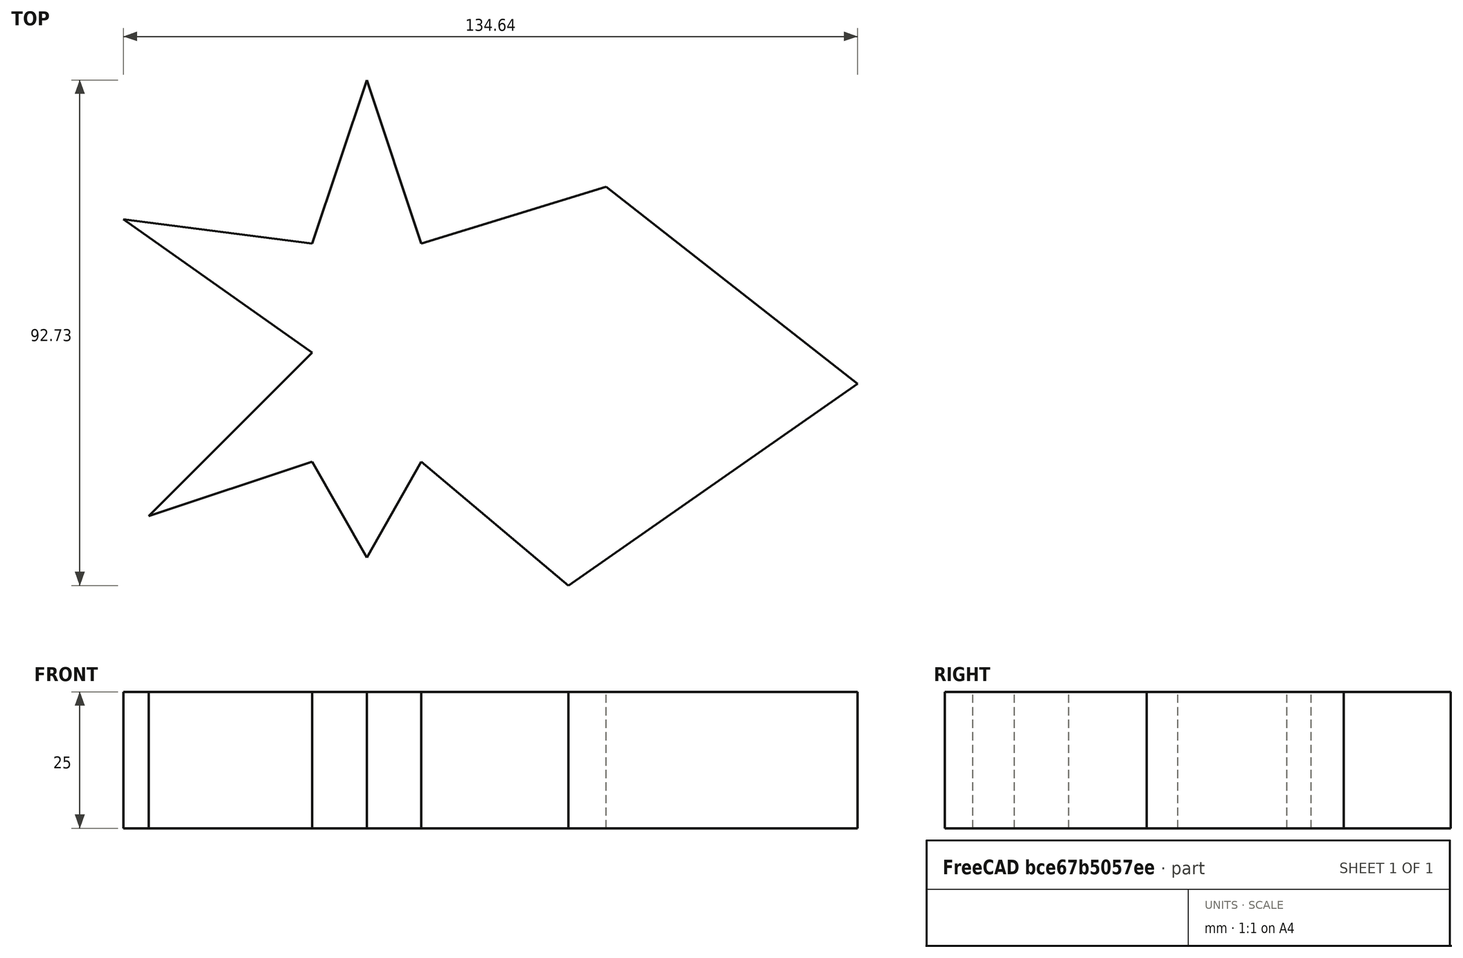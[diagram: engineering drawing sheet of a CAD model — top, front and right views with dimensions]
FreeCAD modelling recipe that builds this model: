
FCSTD DOCUMENT  (FreeCAD 0.18.4R)
Label: tutorial_freecad_ex16_a
License: All rights reserved
LicenseURL: http://en.wikipedia.org/wiki/All_rights_reserved
objects: Sketcher::SketchObject×1, PartDesign::Pad×1, PartDesign::Body×1
note: 4 computed .brp shape members not serialized (recipe doc carries the construction recipe); baked Part::Feature solids carry a one-line shape summary decoded from their .brp

FEATURE [Sketcher::SketchObject] Sketch  label="boceto_estrella"
  MapMode = 5
  Support = -> [XY_Plane]
  sketch-geometry (12):
    g0: LineSegment StartX=0 StartY=50 StartZ=0 EndX=10 EndY=20 EndZ=0
    g1: LineSegment StartX=10 StartY=20 StartZ=0 EndX=43.8533 EndY=30.419 EndZ=0
    g2: LineSegment StartX=43.8533 StartY=30.419 StartZ=0 EndX=90 EndY=-5.74356 EndZ=0
    g3: LineSegment StartX=90 StartY=-5.74356 StartZ=0 EndX=36.976 EndY=-42.7309 EndZ=0
    g4: LineSegment StartX=36.976 StartY=-42.7309 StartZ=0 EndX=10 EndY=-20 EndZ=0
    g5: LineSegment StartX=10 StartY=-20 StartZ=0 EndX=0 EndY=-37.6194 EndZ=0
    g6: LineSegment StartX=0 StartY=-37.6194 StartZ=0 EndX=-10 EndY=-20 EndZ=0
    g7: LineSegment StartX=-10 StartY=-20 StartZ=0 EndX=-40 EndY=-30 EndZ=0
    g8: LineSegment StartX=-40 StartY=-30 StartZ=0 EndX=-10 EndY=0 EndZ=0
    g9: LineSegment StartX=-10 StartY=0 StartZ=0 EndX=-44.6416 EndY=24.4254 EndZ=0
    g10: LineSegment StartX=-44.6416 StartY=24.4254 StartZ=0 EndX=-10 EndY=20 EndZ=0
    g11: LineSegment StartX=-10 StartY=20 StartZ=0 EndX=0 EndY=50 EndZ=0
  constraints (12):
    c: Coincident(g0,g1)
    c: Coincident(g1,g2)
    c: Coincident(g2,g3)
    c: Coincident(g3,g4)
    c: Coincident(g4,g5)
    c: Coincident(g5,g6)
    c: Coincident(g6,g7)
    c: Coincident(g7,g8)
    c: Coincident(g8,g9)
    c: Coincident(g9,g10)
    c: Coincident(g10,g11)
    c: Coincident(g11,g0)
FEATURE [PartDesign::Pad] Pad  label="estrella"
  Length = 25
  Length2 = 100
  Profile = -> Sketch
  Refine = true
  Type = 0
FEATURE [PartDesign::Body] Body
  Group = -> [Sketch,Pad]
  Origin = -> Origin
  Tip = -> Pad
